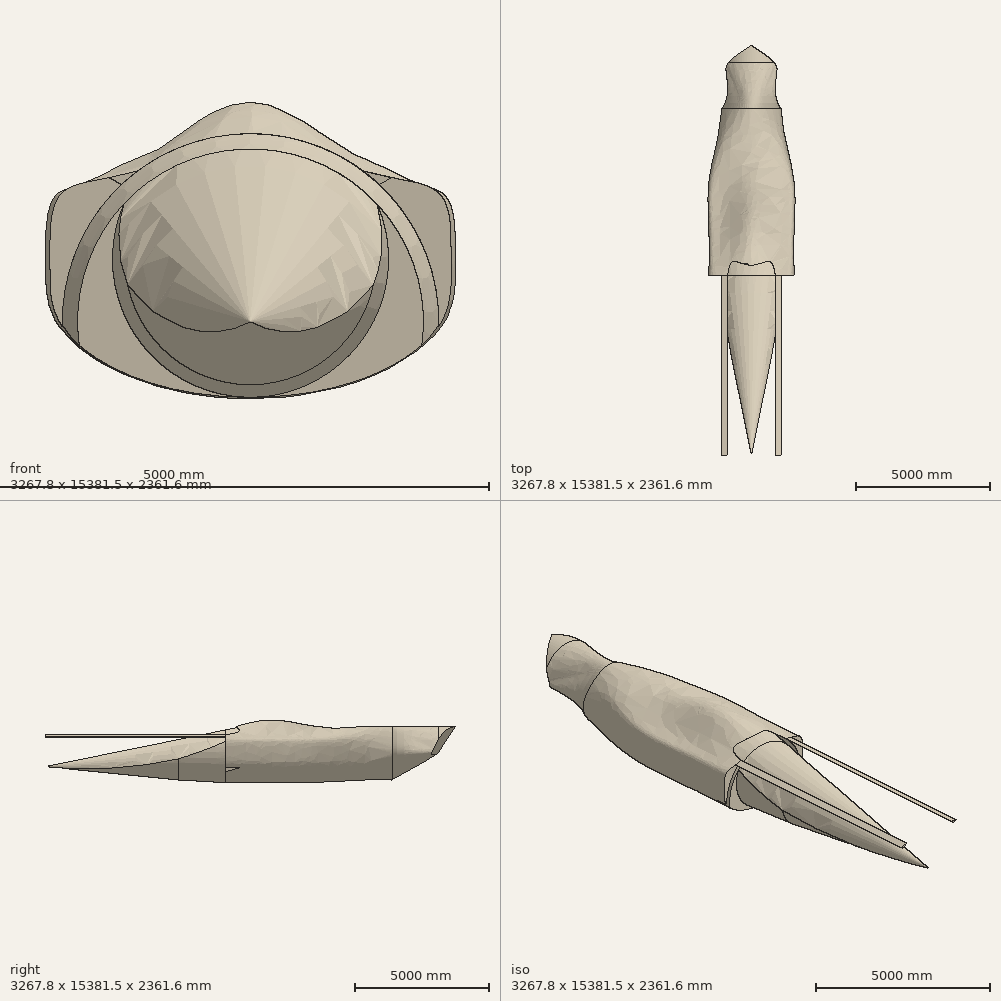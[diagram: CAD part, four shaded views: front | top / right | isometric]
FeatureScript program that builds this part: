
annotation { "Feature Type Name" : "Feature", "Feature Type Description" : "" }
export const myFeature = defineFeature(function(context is Context, id is Id, definition is map)
    precondition{}
    {
        {
            var Q0;
            Q0=qCreatedBy(makeId("Front.planeOp"),FACE);
            cPlane(context, id + "F0", {"entities" : qUnion([Q0]), "cplaneType" : CPlaneType.OFFSET, "offset" : 1750 * mm, "width" : 152.4 * mm, "height" : 152.4 * mm});
        }
        {
            var Q0;
            Q0=qCreatedBy(id+"F0.planeOp",FACE);
            var sketch = newSketch(context, id + "F1", { "sketchPlane" : qUnion([Q0])});
            skPoint(sketch, "E0.middle", {"position": v(0, 0) * mm});
            skFitSpline(sketch, "E1", {"points": [v(0, 877.87) * mm, v(1060, 662.5) * mm, v(1517.6, 506.84) * mm, v(1600, 0) * mm, v(1517.6, -506.84) * mm, v(750, -1000) * mm, v(-750, -1000) * mm, v(-1517.6, -506.84) * mm, v(-1600, 0) * mm, v(-1517.6, 506.84) * mm, v(-1060, 662.5) * mm, v(0, 877.87) * mm]});
            skSolve(sketch);
        }
        {
            var Q0;
            Q0=qCreatedBy(makeId("Front.planeOp"),FACE);
            var sketch = newSketch(context, id + "F2", { "sketchPlane" : qUnion([Q0])});
            skPoint(sketch, "E2.middle", {"position": v(0, 0) * mm});
            skFitSpline(sketch, "E3", {"points": [v(0, 1250) * mm, v(1060, 662.5) * mm, v(1517.6, 506.84) * mm, v(1600, 0) * mm, v(1517.6, -506.84) * mm, v(750, -1000) * mm, v(-750, -1000) * mm, v(-1517.6, -506.84) * mm, v(-1600, 0) * mm, v(-1517.6, 506.84) * mm, v(-1060, 662.5) * mm, v(0, 1250) * mm]});
            skSolve(sketch);
        }
        {
            var Q0;
            Q0=qCreatedBy(makeId("Front.planeOp"),FACE);
            cPlane(context, id + "F3", {"entities" : qUnion([Q0]), "cplaneType" : CPlaneType.OFFSET, "offset" : 1750 * mm, "oppositeDirection" : true, "width" : 150 * mm, "height" : 150 * mm});
        }
        {
            var Q0;
            Q0=qCreatedBy(id+"F3.planeOp",FACE);
            var sketch = newSketch(context, id + "F4", { "sketchPlane" : qUnion([Q0])});
            skPoint(sketch, "E4.middle", {"position": v(0, 0) * mm});
            skFitSpline(sketch, "E5", {"points": [v(0, 1000) * mm, v(1060, 662.5) * mm, v(1517.6, 506.84) * mm, v(1600, 0) * mm, v(1517.6, -506.84) * mm, v(750, -1000) * mm, v(-750, -1000) * mm, v(-1517.6, -506.84) * mm, v(-1600, 0) * mm, v(-1517.6, 506.84) * mm, v(-1060, 662.5) * mm, v(0, 1000) * mm]});
            skSolve(sketch);
        }
        {
            var Q0;
            Q0=qCreatedBy(makeId("Front.planeOp"),FACE);
            cPlane(context, id + "F5", {"entities" : qUnion([Q0]), "cplaneType" : CPlaneType.OFFSET, "offset" : 3500 * mm, "oppositeDirection" : true, "width" : 150 * mm, "height" : 150 * mm});
        }
        {
            var Q0;
            Q0=qCreatedBy(id+"F5.planeOp",FACE);
            var sketch = newSketch(context, id + "F6", { "sketchPlane" : qUnion([Q0])});
            skPoint(sketch, "E6.middle", {"position": v(0, 0) * mm});
            skFitSpline(sketch, "E7", {"points": [v(0, 1000) * mm, v(1060, 662.5) * mm, v(1250, 0) * mm, v(1060, -662.5) * mm, v(0, -1000) * mm, v(-1060, -662.5) * mm, v(-1250, 0) * mm, v(-1060, 662.5) * mm, v(0, 1000) * mm]});
            skSolve(sketch);
        }
        {
            var Q0;
            Q0=qCreatedBy(makeId("Front.planeOp"),FACE);
            cPlane(context, id + "F7", {"entities" : qUnion([Q0]), "cplaneType" : CPlaneType.OFFSET, "offset" : 4500 * mm, "oppositeDirection" : true, "width" : 150 * mm, "height" : 150 * mm});
        }
        {
            var Q0;
            Q0=qCreatedBy(id+"F7.planeOp",FACE);
            var sketch = newSketch(context, id + "F8", { "sketchPlane" : qUnion([Q0])});
            skPoint(sketch, "E8.middle", {"position": v(0, 0) * mm});
            skFitSpline(sketch, "E9", {"points": [v(0, 1000) * mm, v(848, 530) * mm, v(1108.5, 0) * mm, v(848, -530) * mm, v(0, -1000) * mm, v(-848, -530) * mm, v(-1108.5, 0) * mm, v(-848, 530) * mm, v(0, 1000) * mm]});
            skSolve(sketch);
        }
        {
            var Q0;
            Q0=qCreatedBy(makeId("Front.planeOp"),FACE);
            cPlane(context, id + "F9", {"entities" : qUnion([Q0]), "cplaneType" : CPlaneType.OFFSET, "offset" : 6232.05 * mm, "oppositeDirection" : true, "width" : 150 * mm, "height" : 150 * mm});
        }
        {
            var Q0;
            Q0=qCreatedBy(id+"F9.planeOp",FACE);
            var sketch = newSketch(context, id + "F10", { "sketchPlane" : qUnion([Q0])});
            skArc(sketch, "E10", {"start": v(998.61, 52.63) * mm, "mid": v(0, 1000) * mm, "end": v(-998.61, 52.63) * mm});
            skLineSegment(sketch, "E11", {"start": v(0, 0) * mm, "end": v(-948.68, 0) * mm});
            skLineSegment(sketch, "E12", {"start": v(0, 0) * mm, "end": v(948.68, 0) * mm});
            skPoint(sketch, "E13.visualSharp", {"position": v(-1000, 0) * mm});
            skArc(sketch, "E13.filletArc", {"start": v(-998.61, 52.63) * mm, "mid": v(-984.96, 15.59) * mm, "end": v(-948.68, 0) * mm});
            skPoint(sketch, "E14.visualSharp", {"position": v(1000, 0) * mm});
            skArc(sketch, "E14.filletArc", {"start": v(948.68, 0) * mm, "mid": v(984.96, 15.59) * mm, "end": v(998.61, 52.63) * mm});
            skSolve(sketch);
        }
        {
            var Q0;
            Q0=sQuery(id+"F10.wireOp",EDGE,"E11");
            var Q1;
            Q1=sQuery(id+"F8.wireOp",VERTEX,"E9.6.internal");
            cPlane(context, id + "F11", {"entities" : qUnion([Q0, Q1]), "cplaneType" : CPlaneType.LINE_ANGLE, "offset" : 25 * mm, "angle" : 0 * degree, "width" : 150 * mm, "height" : 150 * mm});
        }
        {
            var Q0;
            Q0=qCreatedBy(id+"F11.planeOp",FACE);
            var sketch = newSketch(context, id + "F12", { "sketchPlane" : qUnion([Q0])});
            skFitSpline(sketch, "E15", {"points": [v(-1108.5, 4500) * mm, v(-948.68, 6232.05) * mm], "startDerivative": vector(1200, 1755) * mm, "endDerivative": vector(158.07, 1422.55) * mm});
            skFitSpline(sketch, "E16", {"points": [v(1108.5, 4500) * mm, v(948.68, 6232.05) * mm], "startDerivative": vector(-1200, 1755) * mm, "endDerivative": vector(-158.07, 1422.55) * mm});
            skSolve(sketch);
        }
        {
            var Q0;
            Q0=makeQuery(id+"F1.imprint","IMPRINT",FACE,{"disambiguationData":[TD([[makeQuery(id+"F1.imprint","IMPRINT",EDGE,{"derivedFrom":sQuery(id+"F1.wireOp",EDGE,"E1")}),-1.0]])]});
            var Q1;
            Q1=makeQuery(id+"F2.imprint","IMPRINT",FACE,{"disambiguationData":[TD([[makeQuery(id+"F2.imprint","IMPRINT",EDGE,{"derivedFrom":sQuery(id+"F2.wireOp",EDGE,"E3")}),-1.0]])]});
            var Q2;
            Q2=makeQuery(id+"F4.imprint","IMPRINT",FACE,{"disambiguationData":[TD([[makeQuery(id+"F4.imprint","IMPRINT",EDGE,{"derivedFrom":sQuery(id+"F4.wireOp",EDGE,"E5")}),-1.0]])]});
            var Q3;
            Q3=makeQuery(id+"F6.imprint","IMPRINT",FACE,{"disambiguationData":[TD([[makeQuery(id+"F6.imprint","IMPRINT",EDGE,{"derivedFrom":sQuery(id+"F6.wireOp",EDGE,"E7")}),-1.0]])]});
            var Q4;
            Q4=makeQuery(id+"F8.imprint","IMPRINT",FACE,{"disambiguationData":[TD([[makeQuery(id+"F8.imprint","IMPRINT",EDGE,{"derivedFrom":sQuery(id+"F8.wireOp",EDGE,"E9")}),-1.0]])]});
            loft(context, id + "F13", {"sheetProfilesArray" : [{ "sheetProfileEntities" : qUnion([Q0]) }, { "sheetProfileEntities" : qUnion([Q1]) }, { "sheetProfileEntities" : qUnion([Q2]) }, { "sheetProfileEntities" : qUnion([Q3]) }, { "sheetProfileEntities" : qUnion([Q4]) }]});
        }
        {
            var Q1;
            Q1=makeQuery(id+"F8.imprint","IMPRINT",FACE,{"disambiguationData":[TD([[makeQuery(id+"F8.imprint","IMPRINT",EDGE,{"derivedFrom":sQuery(id+"F8.wireOp",EDGE,"E9")}),-1.0]])]});
            var Q2;
            Q2=makeQuery(id+"F10.imprint","IMPRINT",FACE,{"disambiguationData":[TD([[makeQuery(id+"F10.imprint","IMPRINT",EDGE,{"derivedFrom":sQuery(id+"F10.wireOp",EDGE,"E10")}),1.0]])]});
            var Q3;
            Q3=sQuery(id+"F12.wireOp",EDGE,"E15");
            var Q4;
            Q4=sQuery(id+"F12.wireOp",EDGE,"E16");
            loft(context, id + "F14", {"operationType" : NewBodyOperationType.ADD, "addGuides" : true, "sheetProfilesArray" : [{ "sheetProfileEntities" : qUnion([Q1]) }, { "sheetProfileEntities" : qUnion([Q2]) }], "guidesArray" : [{ "guideEntities" : qUnion([Q3]), "guideDerivativeType" : LoftGuideDerivativeType.DEFAULT, "guideDerivativeMagnitude" : 1 }, { "guideEntities" : qUnion([Q4]), "guideDerivativeType" : LoftGuideDerivativeType.DEFAULT, "guideDerivativeMagnitude" : 1 }]});
        }
        {
            var Q0;
            Q0=qSketchRegion(id+"F1",true);
            extrude(context, id + "F15", {"entities" : qUnion([Q0]), "depth" : 6750 * mm});
        }
        {
            var Q0;
            Q0=qCreatedBy(makeId("Right.planeOp"),FACE);
            var sketch = newSketch(context, id + "F16", { "sketchPlane" : qUnion([Q0])});
            skLineSegment(sketch, "E17", {"start": v(0, 0) * mm, "end": v(-3500, 0) * mm});
            skLineSegment(sketch, "E18", {"start": v(-3500, 0) * mm, "end": v(-3500, -1000) * mm});
            skLineSegment(sketch, "E19", {"start": v(-3500, -1000) * mm, "end": v(-8500, -1000) * mm});
            skLineSegment(sketch, "E20", {"start": v(-8500, -1000) * mm, "end": v(-8500, -499.31) * mm});
            skLineSegment(sketch, "E21", {"start": v(-1151.4, 0) * mm, "end": v(-1151.4, 1000) * mm});
            skLineSegment(sketch, "E22", {"start": v(-1151.4, 1000) * mm, "end": v(-8500, -499.31) * mm});
            skLineSegment(sketch, "E23", {"start": v(-8500, -499.31) * mm, "end": v(-3500, -1000) * mm});
            skLineSegment(sketch, "E24", {"start": v(-3500, 1000) * mm, "end": v(4500, 1000) * mm});
            skLineSegment(sketch, "E25", {"start": v(-3500, 1000) * mm, "end": v(-8500, 1000) * mm});
            skLineSegment(sketch, "E26", {"start": v(-8500, 1000) * mm, "end": v(-8500, -499.31) * mm});
            skLineSegment(sketch, "E27", {"start": v(-8500, -1000) * mm, "end": v(-8500, -1750) * mm});
            skLineSegment(sketch, "E28", {"start": v(-8500, -1750) * mm, "end": v(-1750, -1750) * mm});
            skPoint(sketch, "E28.endSnap0", {"position": v(-1750, 0) * mm});
            skLineSegment(sketch, "E29", {"start": v(-1750, 0) * mm, "end": v(-1750, -1099.92) * mm});
            skLineSegment(sketch, "E30", {"start": v(-1750, -1099.92) * mm, "end": v(-3500, -1000) * mm});
            skLineSegment(sketch, "E31", {"start": v(-1750, -1099.92) * mm, "end": v(-1750, -1750) * mm});
            skLineSegment(sketch, "E32", {"start": v(-8500, -499.31) * mm, "end": v(-3500, -499.31) * mm});
            skSolve(sketch);
        }
        {
            var Q0;
            {var subQ0=sQuery(id+"F16.wireOp",EDGE,"E22");Q0=makeQuery(id+"F16.imprint","IMPRINT",FACE,{"disambiguationData":[TD([[makeQuery(id+"F16.imprint","IMPRINT",EDGE,{"derivedFrom":subQ0}),-1.0]])]});}
            var Q1;
            Q1=sQuery(id+"F16.wireOp",EDGE,"E32");
            revolve(context, id + "F17", {"operationType" : NewBodyOperationType.REMOVE, "entities" : qUnion([Q0]), "axis" : qUnion([Q1]), "revolveType" : RevolveType.SYMMETRIC, "oppositeDirection" : true, "angle" : 250 * degree});
        }
        {
            var Q0;
            Q0=makeQuery(id+"F16.imprint","IMPRINT",FACE,{"disambiguationData":[TD([[makeQuery(id+"F16.imprint","IMPRINT",EDGE,{"derivedFrom":sQuery(id+"F16.wireOp",EDGE,"E19")}),-1.0]])]});
            var Q1;
            Q1=makeQuery(id+"F16.imprint","IMPRINT",FACE,{"disambiguationData":[TD([[makeQuery(id+"F16.imprint","IMPRINT",EDGE,{"derivedFrom":sQuery(id+"F16.wireOp",EDGE,"E19")}),1.0]])]});
            var Q2;
            Q2=sQuery(id+"F16.wireOp",EDGE,"E17");
            revolve(context, id + "F18", {"operationType" : NewBodyOperationType.REMOVE, "entities" : qUnion([Q0, Q1]), "axis" : qUnion([Q2]), "revolveType" : RevolveType.SYMMETRIC, "oppositeDirection" : true, "angle" : 240 * degree});
        }
        {
            var Q0;
            Q0=makeQuery(id+"F14.opLoft","CAP_FACE",FACE,{"disambiguationData":[OSD([makeQuery(id+"F10.imprint","IMPRINT",FACE,{"disambiguationData":[TD([[makeQuery(id+"F10.imprint","IMPRINT",EDGE,{"derivedFrom":sQuery(id+"F10.wireOp",EDGE,"E10")}),1.0]])]})])],"isStart":true});
            extrude(context, id + "F19", {"entities" : qUnion([Q0]), "operationType" : NewBodyOperationType.ADD, "depth" : 649.4 * mm});
        }
        {
            var Q0;
            Q0=qCreatedBy(makeId("Right.planeOp"),FACE);
            var sketch = newSketch(context, id + "F20", { "sketchPlane" : qUnion([Q0])});
            skLineSegment(sketch, "E33", {"start": v(0, 0) * mm, "end": v(4500, 0) * mm});
            skLineSegment(sketch, "E34", {"start": v(4500, 0) * mm, "end": v(6232.05, 0) * mm});
            skLineSegment(sketch, "E35", {"start": v(4500, 0) * mm, "end": v(4500, 1000) * mm});
            skLineSegment(sketch, "E36", {"start": v(4500, 1000) * mm, "end": v(6881.46, 1000) * mm});
            skLineSegment(sketch, "E37", {"start": v(6881.46, 1000) * mm, "end": v(6881.46, -1000) * mm});
            skLineSegment(sketch, "E38", {"start": v(6881.46, 1000) * mm, "end": v(6232.05, 0) * mm});
            skLineSegment(sketch, "E39", {"start": v(6232.05, 0) * mm, "end": v(5582.64, -1000) * mm});
            skLineSegment(sketch, "E40", {"start": v(5582.64, -1000) * mm, "end": v(6881.46, -1000) * mm});
            skSolve(sketch);
        }
        {
            var Q0;
            Q0=makeQuery(id+"F20.imprint","IMPRINT",FACE,{"disambiguationData":[TD([[makeQuery(id+"F20.imprint","IMPRINT",EDGE,{"derivedFrom":sQuery(id+"F20.wireOp",EDGE,"E37")}),-1.0]])]});
            var Q1;
            Q1=sQuery(id+"F20.wireOp",EDGE,"E36");
            revolve(context, id + "F21", {"operationType" : NewBodyOperationType.REMOVE, "entities" : qUnion([Q0]), "axis" : qUnion([Q1]), "revolveType" : RevolveType.SYMMETRIC, "oppositeDirection" : true, "angle" : 182 * degree});
        }
    });
